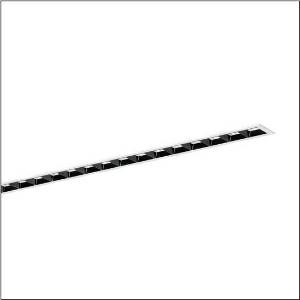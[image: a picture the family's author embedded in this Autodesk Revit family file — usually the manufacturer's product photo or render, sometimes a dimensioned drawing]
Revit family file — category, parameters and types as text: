
# Revit family: silica_r__21_51mx14db35wb_9a50
name_source: partatom
category: Lighting Fixtures
units: mm (PartAtom-declared; Revit-internal decimal feet)

## family parameters
Cut with Voids When Loaded = No
Host = Face
Light Source = No
Part Type = Normal
Room Calculation Point = No
Round Connector Dimension = Use Diameter
Shared = No

## types (1)
- --- (1 x LED, 5400 lm, 40.3 W, 3000K)
    Apparent Load = 40 VA
    CIE Flux Codes = 74 94 99 100 100
    Color Rendering = 80
    Color Temperature = 3000K
    Default Elevation = 1800 mm
    Description = Silica® 21, office luminaire, primary light control with darklight reflector, of PMMA, black, light emission: direct distribution, primary light characteristic: asymmetric, installation type: recessed, LED, rated luminous flux: 5.400lm, luminous efficacy: 134lm/W, light colour: 830, colour temperature: 3000K, with terminal, 3+2-pole, max. 2.5mm², mains connection: 220..240V, AC, 50/60Hz, rated input power: 40.3W, luminaire housing, of aluminium, traffic white (RAL 9016), length: 1.528mm, width: 79mm, height: 53mm, protection rating (complete): IP20, insulation class (complete): insulation class I (protective earthing), certification: CE, permissible operating ambient temperature: 0..+35°C, standard: EN 50419, packaging unit: 1 piece
    Height = 0 mm  [stored 0 ft]
    Lamp = 1 x LED
    Lamp Light Flux = 5400 lm
    Lamp Power = 40.3 W
    Lamp count = 1
    Length = 1527 mm
    Luminous efficacy = 134 lm/W
    Manufacturer = Siteco
    ModVariant = No
    Model = 51MX14DB35WB
    Mounting Place = Ceiling
    Mounting Type = Recessed
    Number of Poles = 1
    OnlyDefault = Yes
    Power Factor = 1
    Product Name = Silica® 21
    Product group = office luminaire | ceiling recessed
    ProductGroupID = 400
    Protection Class = Protection class I
    Protection Degree = IP 20
    RLX_Detail_Level = 1
    RlxData = <blob elided: 42789 chars, md5=6e1eb1dd>
    Socket = socket
    Standby Power = 0 W
    System Light Flux = 5400 lm
    System Power = 40 W
    Type Comments = factory setting: luminous flux: 100 % | dim-lin: 254 | 448 mA
    Type Image = l_1251632.jpg
    URL = http://relux.com
    VarID = @adj_031589
    Voltage = 0 V
    Weight = 0.00 kg
    Width = 79 mm

note: [stored X ft] marks values corroborated as IEEE doubles in the binary element streams (Revit-internal decimal feet)

## geometry (parser evidence)
native form markers: Blend x4, Sweep x9
no freeform markers — native parametric forms only
